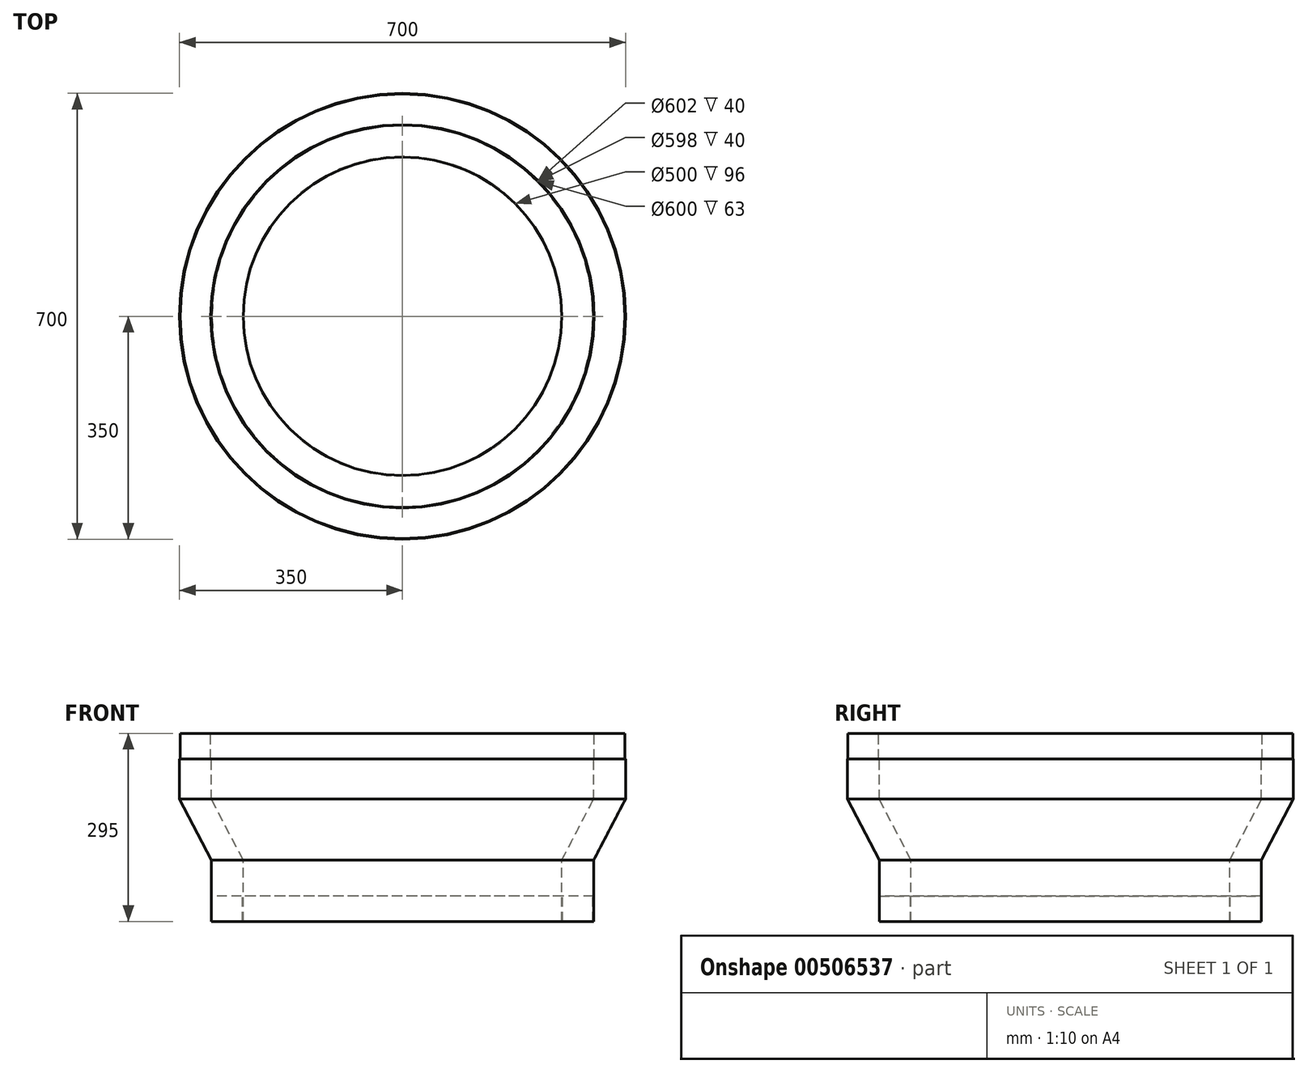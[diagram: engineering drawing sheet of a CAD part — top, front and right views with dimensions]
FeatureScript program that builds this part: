
annotation { "Feature Type Name" : "Feature", "Feature Type Description" : "" }
export const myFeature = defineFeature(function(context is Context, id is Id, definition is map)
    precondition{}
    {
        {
            var Q0;
            Q0=qCreatedBy(makeId("Front.planeOp"),FACE);
            var sketch = newSketch(context, id + "F0", { "sketchPlane" : qUnion([Q0])});
            skLineSegment(sketch, "E0", {"start": v(0, 433.08) * mm, "end": v(0, -434.74) * mm, "construction": true});
            skLineSegment(sketch, "E1", {"start": v(-250, -254.87) * mm, "end": v(-250, -158.87) * mm});
            skLineSegment(sketch, "E2", {"start": v(-250, -254.87) * mm, "end": v(-251, -254.87) * mm});
            skLineSegment(sketch, "E3", {"start": v(-251, -254.87) * mm, "end": v(-251, -214.87) * mm});
            skLineSegment(sketch, "E4", {"start": v(-251, -214.87) * mm, "end": v(-299, -214.87) * mm});
            skLineSegment(sketch, "E5", {"start": v(-299, -214.87) * mm, "end": v(-299, -254.87) * mm});
            skLineSegment(sketch, "E6", {"start": v(-299, -254.87) * mm, "end": v(-300, -254.87) * mm});
            skLineSegment(sketch, "E7", {"start": v(-300, -254.87) * mm, "end": v(-300, -158.87) * mm});
            skLineSegment(sketch, "E8", {"start": v(-349, 40.13) * mm, "end": v(-301, 40.13) * mm});
            skLineSegment(sketch, "E9", {"start": v(-301, 40.13) * mm, "end": v(-301, 0.13) * mm});
            skLineSegment(sketch, "E10", {"start": v(-301, 0.13) * mm, "end": v(-300, 0.13) * mm});
            skLineSegment(sketch, "E11", {"start": v(-300, 0.13) * mm, "end": v(-300, -62.87) * mm});
            skLineSegment(sketch, "E12", {"start": v(-349, 40.13) * mm, "end": v(-349, 0.13) * mm});
            skLineSegment(sketch, "E13", {"start": v(-349, 0.13) * mm, "end": v(-350, 0.13) * mm});
            skLineSegment(sketch, "E14", {"start": v(-350, 0.13) * mm, "end": v(-350, -62.87) * mm});
            skLineSegment(sketch, "E15", {"start": v(-300, -62.87) * mm, "end": v(-250, -158.87) * mm});
            skLineSegment(sketch, "E16", {"start": v(-350, -62.87) * mm, "end": v(-300, -158.87) * mm});
            skSolve(sketch);
        }
        {
            var Q0;
            Q0=qSketchRegion(id+"F0",true);
            var Q1;
            Q1=sQuery(id+"F0.wireOp",EDGE,"E0");
            revolve(context, id + "F1", {"entities" : qUnion([Q0]), "axis" : qUnion([Q1]), "revolveType" : RevolveType.FULL});
        }
    });
